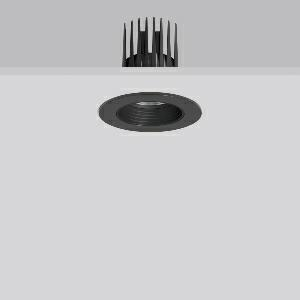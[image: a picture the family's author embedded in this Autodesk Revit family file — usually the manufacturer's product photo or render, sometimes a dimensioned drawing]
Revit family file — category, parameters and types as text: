
# Revit family: heledon_mini_e_901747_003_1_76_f10f
name_source: partatom
category: Lighting Fixtures
units: mm (PartAtom-declared; Revit-internal decimal feet)

## family parameters
Cut with Voids When Loaded = No
Host = Face
Light Source = No
Part Type = Normal
Room Calculation Point = No
Round Connector Dimension = Use Diameter
Shared = No

## types (1)
- HELEDON mini E (1 x LED Modul 940, 2050 lm, 4000)
    Apparent Load = 20 VA
    Approval mark = CE
    CIE Flux Codes = 95 100 100 100 100
    Color Rendering = 92
    Color Temperature = 4000
    Default Elevation = 1800 mm
    Description = Series: HELEDON mini
Round recessed downlight. Housing: die-cast aluminium, powder-coated. Black plastic ring and recessed LED to prevent glare from the side. Optical assembly with lens made of plastic (polycarbonate) for the best homogeneous light distribution - can be changed without tools. Best colour rendering index Ra>90. Suitable for Recessed ceiling mounting. Installation without tools thanks to spring fastening system. Including separate LED converter with connecting cable 600 mm.High quality converter without flickering and stroboscopic effect. Through-wiring box (5 pole) available as accessory. The following accessories can be mounted without use of tools: interchangeable lenses, decorative glasses, honeycomb louvre, clear and frosted diffusers, white interchangeable plastic ring. 
Colour: deep black, matt (RAL 9005)
Diameter: 124 mm
Height: 3 mm
Cut-out diameter: 114 mm
Recess height: 170 mm
Luminaire: recess height: 120 mm
Lamp: LED
Socket: without socket
Colour temperature: 4000K
Colour rendering index (CRI): 92
System power: 20 W
Rated luminous flux: 2050 lm
Luminous efficiency: 103 lm/W
Control gear: Converter, dimmable, DALI
Protection class: II
Type of protection: IP 20
    Height = 0 mm  [stored 0 ft]
    Lamp = 1 x LED Modul 940
    Lamp Light Flux = 2050 lm
    Lamp count = 1
    Length = 124 mm
    Lifetime = 50000 h
    Luminous efficacy = 103 lm/W
    Manufacturer = RZB
    ModVariant = No
    Model = 901747.003.1.76
    Mounting Place = Ceiling
    Mounting Type = Recessed
    Number of Poles = 1
    OnlyDefault = Yes
    Power Factor = 1
    Product Name = HELEDON mini E
    Product group = Recessed downlights
    ProductGroupID = 402
    Protection Class = Protection class II
    Protection Degree = IP 20
    RLX_Detail_Level = 1
    RLX_Emergency_Light_Flux = 0 lm
    RLX_Emergency_Type = 0
    RLX_Emergency_Type_DB = No
    RlxData = <blob elided: 134121 chars, md5=d0e485e6>
    Socket = socket
    Standby Power = 0 W
    System Light Flux = 2050 lm
    System Power = 20 W
    Type Comments = Product without accessories
    Type Image = 901656.003.jpg
    URL = http://relux.com
    VarID = ---
    Voltage = 230 V
    Voltage Range = 220-240 V
    Weight = 0.00 kg
    Width = 0 mm  [stored 0 ft]

note: [stored X ft] marks values corroborated as IEEE doubles in the binary element streams (Revit-internal decimal feet)

## geometry (parser evidence)
native form markers: Blend x4, Sweep x9
no freeform markers — native parametric forms only
